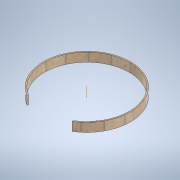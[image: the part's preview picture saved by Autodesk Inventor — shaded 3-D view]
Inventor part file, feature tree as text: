
AUTODESK INVENTOR PART (.ipt)
format: ipt  version: 2020 (Build 240168000, 168)  size: 204,288 bytes
history: native  units: mm
features: extrude x2, sketch x1
ambient origin geometry x8: Origin, YZ Plane, XZ Plane, XY Plane, X Axis, Y Axis, Z Axis, Center Point
bodies: Body1 (feature_tree)
feature tree (3):
  extrude  "Extrusion3"  Depth=10.0mm
  extrude  "Extrusion5"  Depth=10.0mm
  sketch  "Sketch3"  dims[d15=30.0mm d16=0.0mm d40=3.25mm d52=4.363323mm d54=10.0mm d55=0.0mm d60=0.872665mm d61=12.566371mm d62=13.439035mm d87=145.0mm d88=345.36mm d89=4.363323mm d90=1.919862mm d91=1.919862mm d169=292.14mm d170=300.14mm]
